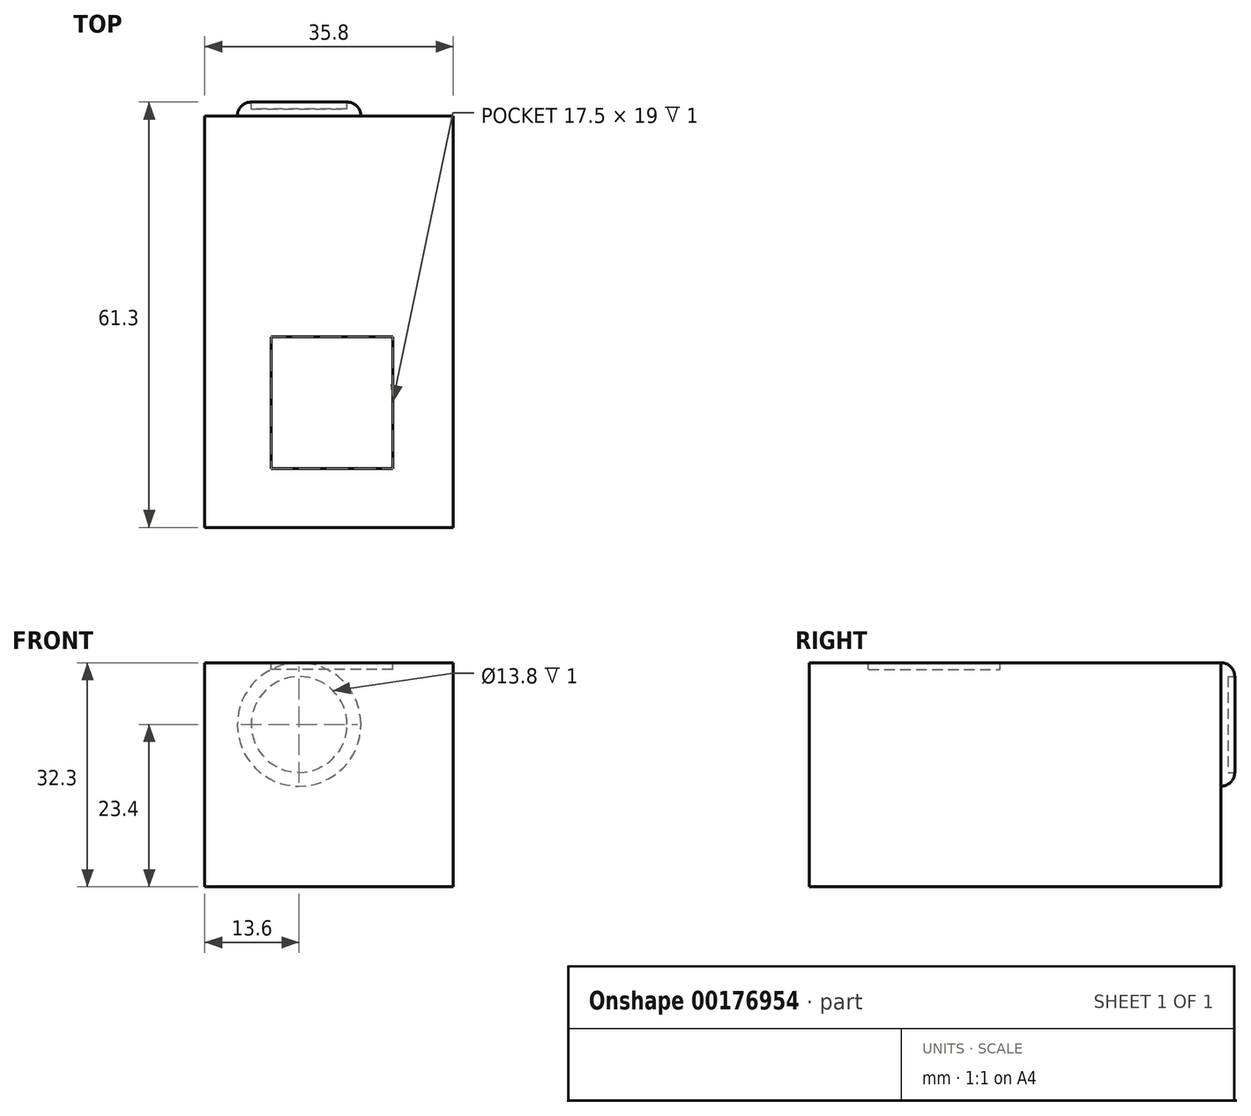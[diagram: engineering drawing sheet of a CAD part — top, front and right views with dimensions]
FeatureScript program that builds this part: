
annotation { "Feature Type Name" : "Feature", "Feature Type Description" : "" }
export const myFeature = defineFeature(function(context is Context, id is Id, definition is map)
    precondition{}
    {
        {
            var Q0;
            Q0=qCreatedBy(makeId("Top.planeOp"),FACE);
            var sketch = newSketch(context, id + "F0", { "sketchPlane" : qUnion([Q0])});
            skLineSegment(sketch, "E0.bottom", {"start": v(-17.9, 29.65) * mm, "end": v(17.9, 29.65) * mm});
            skLineSegment(sketch, "E0.top", {"start": v(-17.9, -29.65) * mm, "end": v(17.9, -29.65) * mm});
            skLineSegment(sketch, "E0.left", {"start": v(-17.9, 29.65) * mm, "end": v(-17.9, -29.65) * mm});
            skLineSegment(sketch, "E0.right", {"start": v(17.9, 29.65) * mm, "end": v(17.9, -29.65) * mm});
            skPoint(sketch, "E0.middle", {"position": v(0, 0) * mm});
            skSolve(sketch);
        }
        {
            var Q0;
            Q0 = qSketchRegion(id + "F0", true);
            extrude(context, id + "F1", {"entities" : qUnion([Q0]), "depth" : 32.3 * mm});
        }
        {
            var Q0;
            Q0=makeQuery(id+"F1.opExtrude","CAP_FACE",FACE,{"disambiguationData":[OSD([sQuery(id+"F0.wireOp",EDGE,"E0.bottom"),sQuery(id+"F0.wireOp",EDGE,"E0.top"),sQuery(id+"F0.wireOp",EDGE,"E0.left"),sQuery(id+"F0.wireOp",EDGE,"E0.right")])],"isStart":false});
            var sketch = newSketch(context, id + "F2", { "sketchPlane" : qUnion([Q0])});
            skLineSegment(sketch, "E1.bottom", {"start": v(9.2, -21.15) * mm, "end": v(-8.3, -21.15) * mm});
            skLineSegment(sketch, "E1.top", {"start": v(9.2, -2.15) * mm, "end": v(-8.3, -2.15) * mm});
            skLineSegment(sketch, "E1.left", {"start": v(9.2, -21.15) * mm, "end": v(9.2, -2.15) * mm});
            skLineSegment(sketch, "E1.right", {"start": v(-8.3, -21.15) * mm, "end": v(-8.3, -2.15) * mm});
            skPoint(sketch, "E1.middle", {"position": v(0.45, -11.65) * mm});
            skSolve(sketch);
        }
        {
            var Q0;
            Q0=makeQuery(id+"F2.imprint","IMPRINT",FACE,{"disambiguationData":[TD([[makeQuery(id+"F2.imprint","IMPRINT",EDGE,{"derivedFrom":sQuery(id+"F2.wireOp",EDGE,"E1.bottom")}),-1.0]])]});
            extrude(context, id + "F3", {"entities" : qUnion([Q0]), "operationType" : NewBodyOperationType.REMOVE, "oppositeDirection" : true, "depth" : 1 * mm});
        }
        {
            var Q0;
            Q0=makeQuery(id+"F1.opExtrude","SWEPT_FACE",FACE,{"disambiguationData":[OSD([sQuery(id+"F0.wireOp",EDGE,"E0.bottom")])]});
            var sketch = newSketch(context, id + "F4", { "sketchPlane" : qUnion([Q0])});
            skCircle(sketch, "E2", {"center": v(4.3, 23.4) * mm, "radius": 8.9 * mm});
            skSolve(sketch);
        }
        {
            var Q0;
            Q0=makeQuery(id+"F4.imprint","IMPRINT",FACE,{"disambiguationData":[TD([[makeQuery(id+"F4.imprint","IMPRINT",EDGE,{"derivedFrom":sQuery(id+"F4.wireOp",EDGE,"E2")}),1.0]])]});
            extrude(context, id + "F5", {"entities" : qUnion([Q0]), "operationType" : NewBodyOperationType.ADD, "depth" : 2 * mm});
        }
        {
            var Q0;
            Q0=makeQuery(id+"F5.opExtrude","CAP_EDGE",EDGE,{"disambiguationData":[OSD([sQuery(id+"F4.wireOp",EDGE,"E2")])],"isStart":false});
            fillet(context, id + "F6", {"entities" : qUnion([Q0]), "radius" : 2 * mm, "tangentPropagation" : true, "allowEdgeOverflow" : false});
        }
        {
            var Q0;
            Q0=makeQuery(id+"F5.opExtrude","CAP_FACE",FACE,{"disambiguationData":[OSD([sQuery(id+"F4.wireOp",EDGE,"E2")])],"isStart":false});
            extrude(context, id + "F7", {"entities" : qUnion([Q0]), "operationType" : NewBodyOperationType.REMOVE, "oppositeDirection" : true, "depth" : 1 * mm});
        }
    });
